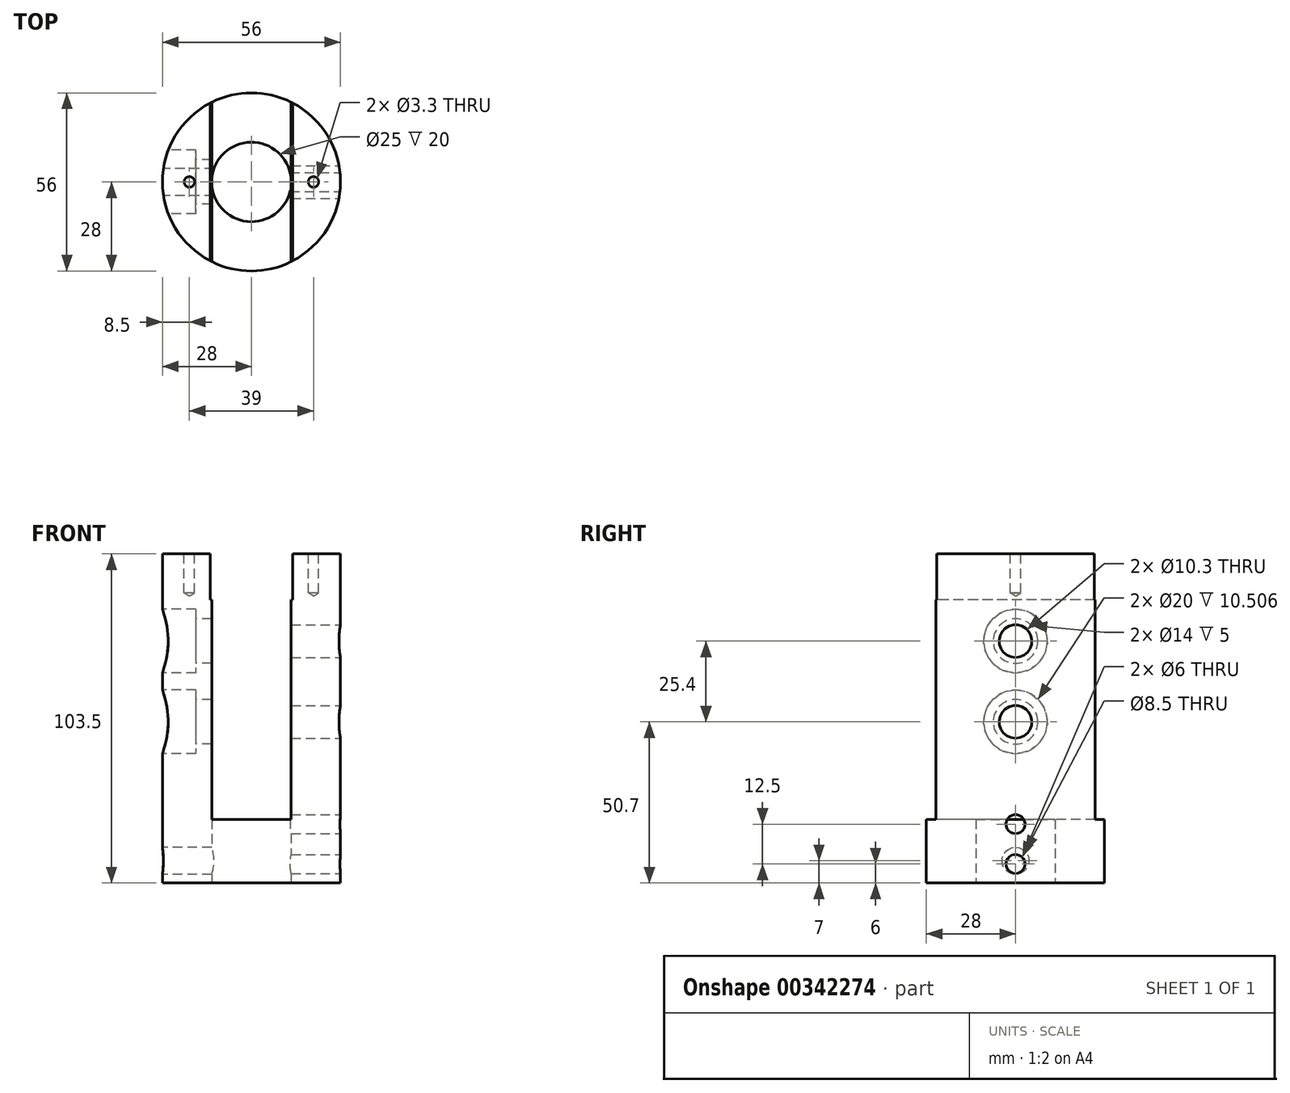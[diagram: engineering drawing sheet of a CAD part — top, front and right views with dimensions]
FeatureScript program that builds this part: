
annotation { "Feature Type Name" : "Feature", "Feature Type Description" : "" }
export const myFeature = defineFeature(function(context is Context, id is Id, definition is map)
    precondition{}
    {
        {
            var Q0;
            Q0=qCreatedBy(makeId("Top.planeOp"),FACE);
            var sketch = newSketch(context, id + "F0", { "sketchPlane" : qUnion([Q0])});
            skCircle(sketch, "E0", {"center": v(0, 0) * mm, "radius": 28 * mm});
            skCircle(sketch, "E1", {"center": v(0, 0) * mm, "radius": 12.5 * mm});
            skSolve(sketch);
        }
        {
            var Q0;
            Q0=makeQuery(id+"F0.imprint","IMPRINT",FACE,{"disambiguationData":[TD([[makeQuery(id+"F0.imprint","IMPRINT",EDGE,{"derivedFrom":sQuery(id+"F0.wireOp",EDGE,"E0")}),1.0]])]});
            extrude(context, id + "F1", {"entities" : qUnion([Q0]), "depth" : 103.5 * mm});
        }
        {
            var Q0;
            Q0=qCreatedBy(makeId("Front.planeOp"),FACE);
            var sketch = newSketch(context, id + "F2", { "sketchPlane" : qUnion([Q0])});
            skLineSegment(sketch, "E2", {"start": v(0, 103.5) * mm, "end": v(0, 0) * mm, "construction": true});
            skLineSegment(sketch, "E3", {"start": v(0, 103.5) * mm, "end": v(-13, 103.5) * mm});
            skLineSegment(sketch, "E4", {"start": v(-13, 103.5) * mm, "end": v(-13, 89.1) * mm});
            skLineSegment(sketch, "E5", {"start": v(-13, 89.1) * mm, "end": v(-12.5, 89.1) * mm});
            skLineSegment(sketch, "E6", {"start": v(-12.5, 89.1) * mm, "end": v(-12.5, 20) * mm});
            skLineSegment(sketch, "E7", {"start": v(0, 20) * mm, "end": v(-12.5, 20) * mm});
            skLineSegment(sketch, "E8.MirrorCS", {"start": v(0, 103.5) * mm, "end": v(13, 103.5) * mm});
            skLineSegment(sketch, "E9.MirrorCS", {"start": v(13, 103.5) * mm, "end": v(13, 89.1) * mm});
            skLineSegment(sketch, "E10.MirrorCS", {"start": v(13, 89.1) * mm, "end": v(12.5, 89.1) * mm});
            skLineSegment(sketch, "E11.MirrorCS", {"start": v(12.5, 89.1) * mm, "end": v(12.5, 20) * mm});
            skLineSegment(sketch, "E12.MirrorCS", {"start": v(0, 20) * mm, "end": v(12.5, 20) * mm});
            skSolve(sketch);
        }
        {
            var Q0;
            Q0 = qSketchRegion(id + "F2", true);
            extrude(context, id + "F3", {"entities" : qUnion([Q0]), "operationType" : NewBodyOperationType.REMOVE, "endBound" : BoundingType.SYMMETRIC, "oppositeDirection" : true, "depth" : 57 * mm});
        }
        {
            var Q0;
            {var subQ0=sQuery(id+"F0.wireOp",EDGE,"E0");Q0=makeQuery(id+"F3.boolean.opBoolean","SPLIT",FACE,{"disambiguationData":[TD([makeQuery(id+"F3.opExtrude","SWEPT_FACE",FACE,{"disambiguationData":[OSD([sQuery(id+"F2.wireOp",EDGE,"E4")])]})])],"derivedFrom":makeQuery(id+"F1.opExtrude","CAP_FACE",FACE,{"disambiguationData":[OSD([subQ0,sQuery(id+"F0.wireOp",EDGE,"E1")])],"isStart":false})});}
            var sketch = newSketch(context, id + "F4", { "sketchPlane" : qUnion([Q0])});
            skCircle(sketch, "E13", {"center": v(-19.5, 0) * mm, "radius": 1.65 * mm});
            skLineSegment(sketch, "E14", {"start": v(0, 24.58) * mm, "end": v(0, -25.57) * mm, "construction": true});
            skCircle(sketch, "E15.MirrorC", {"center": v(19.5, 0) * mm, "radius": 1.65 * mm});
            skSolve(sketch);
        }
        {
            var Q0;
            Q0=sQuery(id+"F4.wireOp",VERTEX,"E13.center");
            var Q1;
            Q1=sQuery(id+"F4.wireOp",VERTEX,"E15.MirrorC.center");
            var Q2;
            Q2=makeQuery(id+"F1.opExtrude","SWEPT_BODY",BODY,{"disambiguationData":[OSD([sQuery(id+"F0.wireOp",EDGE,"E0"),sQuery(id+"F0.wireOp",EDGE,"E1")])]});
            hole(context, id + "F5", {"style" : HoleStyle.SIMPLE, "endStyle" : HoleEndStyle.BLIND, "standardTappedOrClearance" : lookupTablePath({ "standard" : "ISO", "engagement" : "75%", "pitch" : "0.75 mm", "size" : "M4", "type" : "Gewinde" }), "standardBlindInLast" : lookupTablePath({ "standard" : "ISO", "engagement" : "75%", "pitch" : "0.75 mm", "size" : "M4", "type" : "Gewinde" }), "holeDiameter" : 3.3 * mm, "showTappedDepth" : true, "holeDepth" : 12.25 * mm, "isTappedThrough" : true, "tappedDepth" : 10 * mm, "tapClearance" : 3, "locations" : qUnion([Q0, Q1]), "scope" : qUnion([Q2])});
        }
        {
            var Q0;
            Q0=makeQuery(id+"F3.boolean.opBoolean","COPY",FACE,{"derivedFrom":makeQuery(id+"F3.opExtrude","SWEPT_FACE",FACE,{"disambiguationData":[OSD([sQuery(id+"F2.wireOp",EDGE,"E6")])]})});
            cPlane(context, id + "F6", {"entities" : qUnion([Q0]), "cplaneType" : CPlaneType.OFFSET, "offset" : 15.5 * mm, "oppositeDirection" : true, "width" : 150 * mm, "height" : 150 * mm});
        }
        {
            var Q0;
            Q0=makeQuery(id+"F3.boolean.opBoolean","COPY",FACE,{"derivedFrom":makeQuery(id+"F3.opExtrude","SWEPT_FACE",FACE,{"disambiguationData":[OSD([sQuery(id+"F2.wireOp",EDGE,"E11.MirrorCS")])]})});
            cPlane(context, id + "F7", {"entities" : qUnion([Q0]), "cplaneType" : CPlaneType.OFFSET, "offset" : 15.5 * mm, "oppositeDirection" : true, "width" : 150 * mm, "height" : 150 * mm});
        }
        {
            var Q0;
            Q0=qCreatedBy(id+"F6.planeOp",FACE);
            var sketch = newSketch(context, id + "F8", { "sketchPlane" : qUnion([Q0])});
            skCircle(sketch, "E16", {"center": v(0, 7) * mm, "radius": 4.25 * mm});
            skCircle(sketch, "E17", {"center": v(0, 50.7) * mm, "radius": 7 * mm});
            skCircle(sketch, "E18", {"center": v(0, 76.1) * mm, "radius": 7 * mm});
            skSolve(sketch);
        }
        {
            var Q0;
            Q0=qCreatedBy(id+"F7.planeOp",FACE);
            var sketch = newSketch(context, id + "F9", { "sketchPlane" : qUnion([Q0])});
            skCircle(sketch, "E19", {"center": v(0, 50.7) * mm, "radius": 5.15 * mm});
            skCircle(sketch, "E20", {"center": v(0, 76.1) * mm, "radius": 5.15 * mm});
            skCircle(sketch, "E21", {"center": v(0, 6) * mm, "radius": 3 * mm});
            skCircle(sketch, "E22", {"center": v(0, 18.5) * mm, "radius": 3 * mm});
            skSolve(sketch);
        }
        {
            var Q0;
            Q0=sQuery(id+"F8.wireOp",VERTEX,"E16.center");
            var Q1;
            Q1=makeQuery(id+"F1.opExtrude","SWEPT_BODY",BODY,{"disambiguationData":[OSD([sQuery(id+"F0.wireOp",EDGE,"E0"),sQuery(id+"F0.wireOp",EDGE,"E1")])]});
            hole(context, id + "F10", {"style" : HoleStyle.SIMPLE, "endStyle" : HoleEndStyle.BLIND, "oppositeDirection" : true, "standardTappedOrClearance" : lookupTablePath({ "standard" : "ISO", "engagement" : "75%", "pitch" : "1.5 mm", "size" : "M10", "type" : "Gewinde" }), "standardBlindInLast" : lookupTablePath({ "standard" : "ISO", "engagement" : "75%", "pitch" : "1.5 mm", "size" : "M10", "type" : "Gewinde" }), "holeDiameter" : 8.5 * mm, "showTappedDepth" : true, "holeDepth" : 28 * mm, "isTappedThrough" : true, "tappedDepth" : 23.5 * mm, "tapClearance" : 3, "locations" : qUnion([Q0]), "scope" : qUnion([Q1])});
        }
        {
            var Q0;
            Q0=sQuery(id+"F9.wireOp",VERTEX,"E19.center");
            var Q1;
            Q1=sQuery(id+"F9.wireOp",VERTEX,"E20.center");
            var Q2;
            Q2=makeQuery(id+"F1.opExtrude","SWEPT_BODY",BODY,{"disambiguationData":[OSD([sQuery(id+"F0.wireOp",EDGE,"E0"),sQuery(id+"F0.wireOp",EDGE,"E1")])]});
            hole(context, id + "F11", {"style" : HoleStyle.SIMPLE, "endStyle" : HoleEndStyle.BLIND, "oppositeDirection" : true, "standardTappedOrClearance" : lookupTablePath({ "standard" : "ISO", "engagement" : "75%", "pitch" : "1.75 mm", "size" : "M12", "type" : "Gewinde" }), "standardBlindInLast" : lookupTablePath({ "standard" : "ISO", "engagement" : "75%", "pitch" : "1.75 mm", "size" : "M12", "type" : "Gewinde" }), "holeDiameter" : 10.3 * mm, "showTappedDepth" : true, "holeDepth" : 28.75 * mm, "isTappedThrough" : true, "tappedDepth" : 23.5 * mm, "tapClearance" : 3, "startFromSketch" : true, "locations" : qUnion([Q0, Q1]), "scope" : qUnion([Q2])});
        }
        {
            var Q0;
            Q0=qCreatedBy(id+"F6.planeOp",FACE);
            var sketch = newSketch(context, id + "F12", { "sketchPlane" : qUnion([Q0])});
            skCircle(sketch, "E23", {"center": v(0, 50.7) * mm, "radius": 7 * mm});
            skCircle(sketch, "E24", {"center": v(0, 76.1) * mm, "radius": 7 * mm});
            skSolve(sketch);
        }
        {
            var Q0;
            Q0=sQuery(id+"F12.wireOp",VERTEX,"E24.center");
            var Q1;
            Q1=sQuery(id+"F12.wireOp",VERTEX,"E23.center");
            var Q2;
            Q2=makeQuery(id+"F1.opExtrude","SWEPT_BODY",BODY,{"disambiguationData":[OSD([sQuery(id+"F0.wireOp",EDGE,"E0"),sQuery(id+"F0.wireOp",EDGE,"E1")])]});
            hole(context, id + "F13", {"style" : HoleStyle.C_BORE, "endStyle" : HoleEndStyle.BLIND, "oppositeDirection" : true, "standardTappedOrClearance" : lookupTablePath({ "standard" : "ISO", "engagement" : "75%", "pitch" : "1.75 mm", "size" : "M12", "type" : "Gewinde" }), "standardBlindInLast" : lookupTablePath({ "standard" : "ISO", "engagement" : "75%", "pitch" : "1.75 mm", "size" : "M12", "type" : "Gewinde" }), "holeDiameter" : 14 * mm, "cBoreDiameter" : 20 * mm, "cBoreDepth" : 10.5 * mm, "showTappedDepth" : true, "holeDepth" : 28.75 * mm, "isTappedThrough" : true, "tappedDepth" : 23.5 * mm, "tapClearance" : 3, "startFromSketch" : true, "locations" : qUnion([Q0, Q1]), "scope" : qUnion([Q2])});
        }
        {
            var Q0;
            Q0=qCreatedBy(id+"F7.planeOp",FACE);
            var sketch = newSketch(context, id + "F14", { "sketchPlane" : qUnion([Q0])});
            skCircle(sketch, "E25", {"center": v(0, 6) * mm, "radius": 3 * mm});
            skCircle(sketch, "E26", {"center": v(0, 18.5) * mm, "radius": 3 * mm});
            skSolve(sketch);
        }
        {
            var Q0;
            Q0=sQuery(id+"F14.wireOp",VERTEX,"E26.center");
            var Q1;
            Q1=sQuery(id+"F14.wireOp",VERTEX,"E25.center");
            var Q2;
            Q2=makeQuery(id+"F1.opExtrude","SWEPT_BODY",BODY,{"disambiguationData":[OSD([sQuery(id+"F0.wireOp",EDGE,"E0"),sQuery(id+"F0.wireOp",EDGE,"E1")])]});
            hole(context, id + "F15", {"style" : HoleStyle.SIMPLE, "endStyle" : HoleEndStyle.BLIND, "oppositeDirection" : true, "standardTappedOrClearance" : lookupTablePath({ "standard" : "Benutzerdefiniert" }), "standardBlindInLast" : lookupTablePath({ "standard" : "Benutzerdefiniert" }), "holeDiameter" : 6 * mm, "holeDepth" : 28.75 * mm, "isTappedThrough" : true, "tappedDepth" : 23.5 * mm, "tapClearance" : 3, "startFromSketch" : true, "locations" : qUnion([Q0, Q1]), "scope" : qUnion([Q2])});
        }
    });
